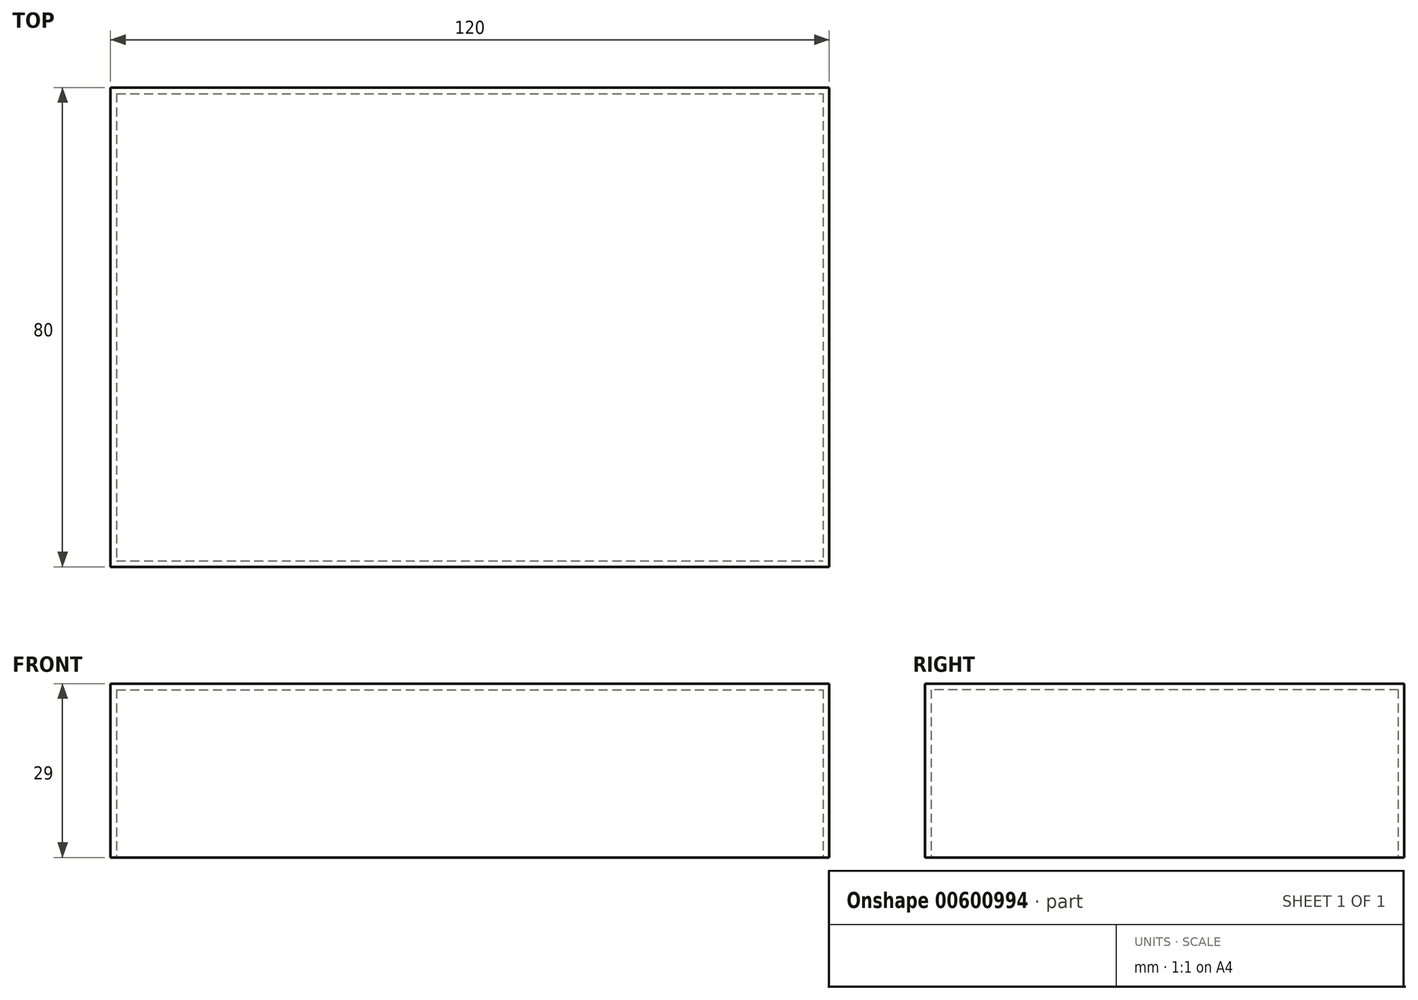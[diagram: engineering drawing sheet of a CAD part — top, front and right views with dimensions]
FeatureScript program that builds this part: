
annotation { "Feature Type Name" : "Feature", "Feature Type Description" : "" }
export const myFeature = defineFeature(function(context is Context, id is Id, definition is map)
    precondition{}
    {
        {
            var Q0;
            Q0=qCreatedBy(makeId("Top.planeOp"),FACE);
            var sketch = newSketch(context, id + "F0", { "sketchPlane" : qUnion([Q0])});
            skLineSegment(sketch, "E0.bottom", {"start": v(-60, 40) * mm, "end": v(60, 40) * mm});
            skLineSegment(sketch, "E0.top", {"start": v(-60, -40) * mm, "end": v(60, -40) * mm});
            skLineSegment(sketch, "E0.left", {"start": v(-60, 40) * mm, "end": v(-60, -40) * mm});
            skLineSegment(sketch, "E0.right", {"start": v(60, 40) * mm, "end": v(60, -40) * mm});
            skPoint(sketch, "E0.middle", {"position": v(0, 0) * mm});
            skSolve(sketch);
        }
        {
            var Q0;
            Q0=makeQuery(id+"F0.imprint","IMPRINT",FACE,{"disambiguationData":[TD([[makeQuery(id+"F0.imprint","IMPRINT",EDGE,{"derivedFrom":sQuery(id+"F0.wireOp",EDGE,"E0.bottom")}),-1.0]])]});
            extrude(context, id + "F1", {"entities" : qUnion([Q0]), "depth" : 29 * mm, "offsetDistance" : 25 * mm});
        }
        {
            var Q0;
            Q0=qCreatedBy(makeId("Top.planeOp"),FACE);
            var sketch = newSketch(context, id + "F2", { "sketchPlane" : qUnion([Q0])});
            skLineSegment(sketch, "E1.bottom", {"start": v(-59, 39) * mm, "end": v(59, 39) * mm});
            skLineSegment(sketch, "E1.top", {"start": v(-59, -39) * mm, "end": v(59, -39) * mm});
            skLineSegment(sketch, "E1.left", {"start": v(-59, 39) * mm, "end": v(-59, -39) * mm});
            skLineSegment(sketch, "E1.right", {"start": v(59, 39) * mm, "end": v(59, -39) * mm});
            skPoint(sketch, "E1.middle", {"position": v(0, 0) * mm});
            skSolve(sketch);
        }
        {
            var Q0;
            Q0 = qSketchRegion(id + "F2", true);
            extrude(context, id + "F3", {"entities" : qUnion([Q0]), "operationType" : NewBodyOperationType.REMOVE, "depth" : 28 * mm, "offsetDistance" : 25 * mm});
        }
    });
